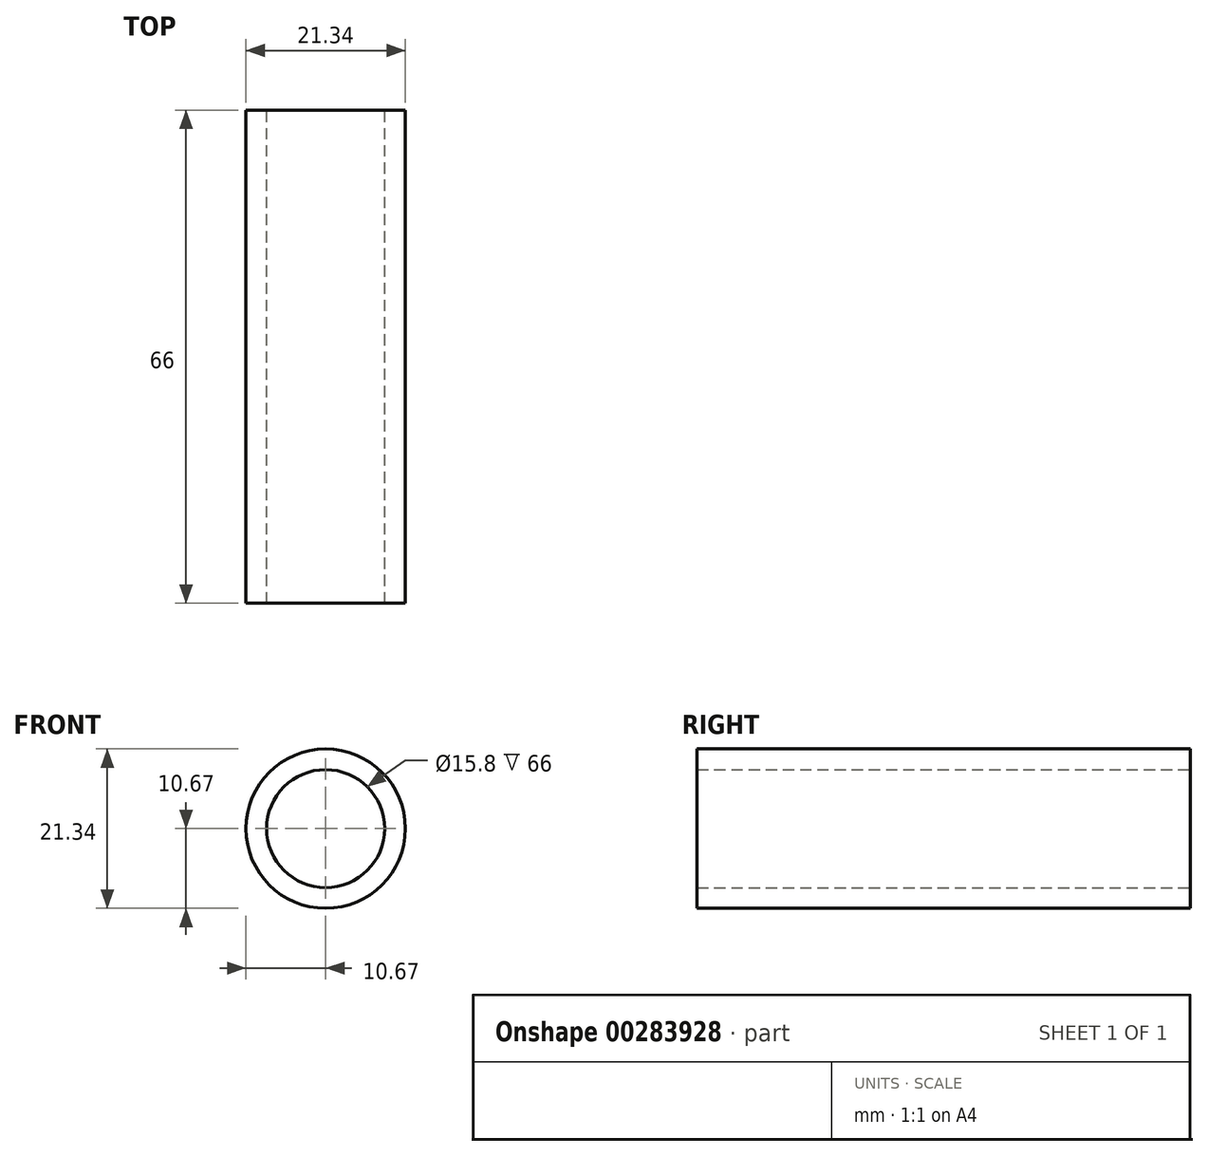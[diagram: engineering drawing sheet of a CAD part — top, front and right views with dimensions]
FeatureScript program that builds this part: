
annotation { "Feature Type Name" : "Feature", "Feature Type Description" : "" }
export const myFeature = defineFeature(function(context is Context, id is Id, definition is map)
    precondition{}
    {
        {
            var Q0;
            Q0=qCreatedBy(makeId("Front.planeOp"),FACE);
            var sketch = newSketch(context, id + "F0", { "sketchPlane" : qUnion([Q0])});
            skCircle(sketch, "E0", {"center": v(0, 0) * mm, "radius": 7.9 * mm});
            skCircle(sketch, "E1", {"center": v(0, 0) * mm, "radius": 10.67 * mm});
            skSolve(sketch);
        }
        {
            var Q0;
            Q0=qSketchRegion(id+"F0",true);
            extrude(context, id + "F1", {"entities" : qUnion([Q0]), "endBound" : BoundingType.SYMMETRIC, "depth" : 66 * mm});
        }
    });
